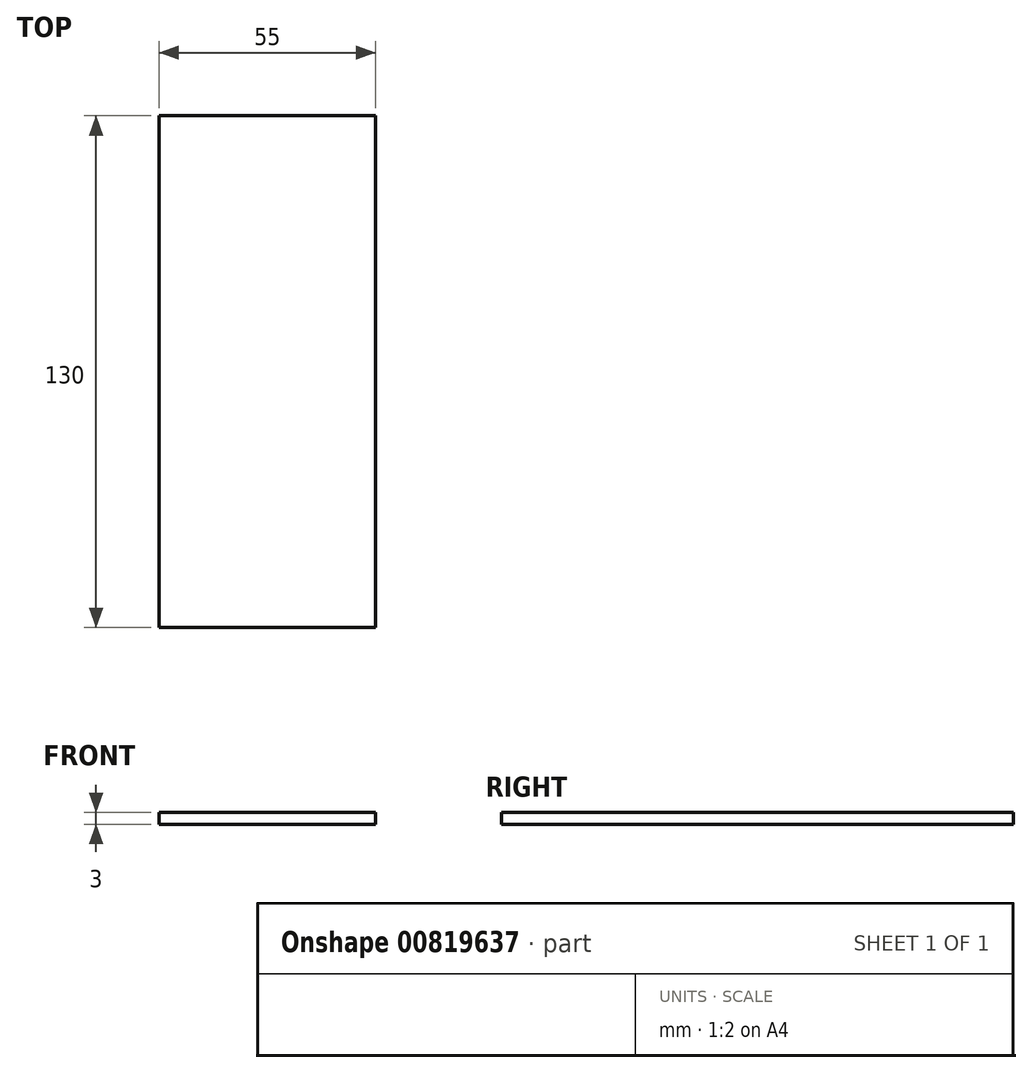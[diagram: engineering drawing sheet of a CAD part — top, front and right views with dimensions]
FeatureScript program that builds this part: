
annotation { "Feature Type Name" : "Feature", "Feature Type Description" : "" }
export const myFeature = defineFeature(function(context is Context, id is Id, definition is map)
    precondition{}
    {
        {
            var Q0;
            Q0=qCreatedBy(makeId("Top.planeOp"),FACE);
            var sketch = newSketch(context, id + "F0", { "sketchPlane" : qUnion([Q0])});
            skLineSegment(sketch, "E0.bottom", {"start": v(0, 0) * mm, "end": v(55, 0) * mm});
            skLineSegment(sketch, "E0.top", {"start": v(0, 130) * mm, "end": v(55, 130) * mm});
            skLineSegment(sketch, "E0.left", {"start": v(0, 0) * mm, "end": v(0, 130) * mm});
            skLineSegment(sketch, "E0.right", {"start": v(55, 0) * mm, "end": v(55, 130) * mm});
            skSolve(sketch);
        }
        {
            var Q0;
            Q0 = qSketchRegion(id + "F0", true);
            extrude(context, id + "F1", {"entities" : qUnion([Q0]), "depth" : 3 * mm, "offsetDistance" : 25 * mm});
        }
    });
